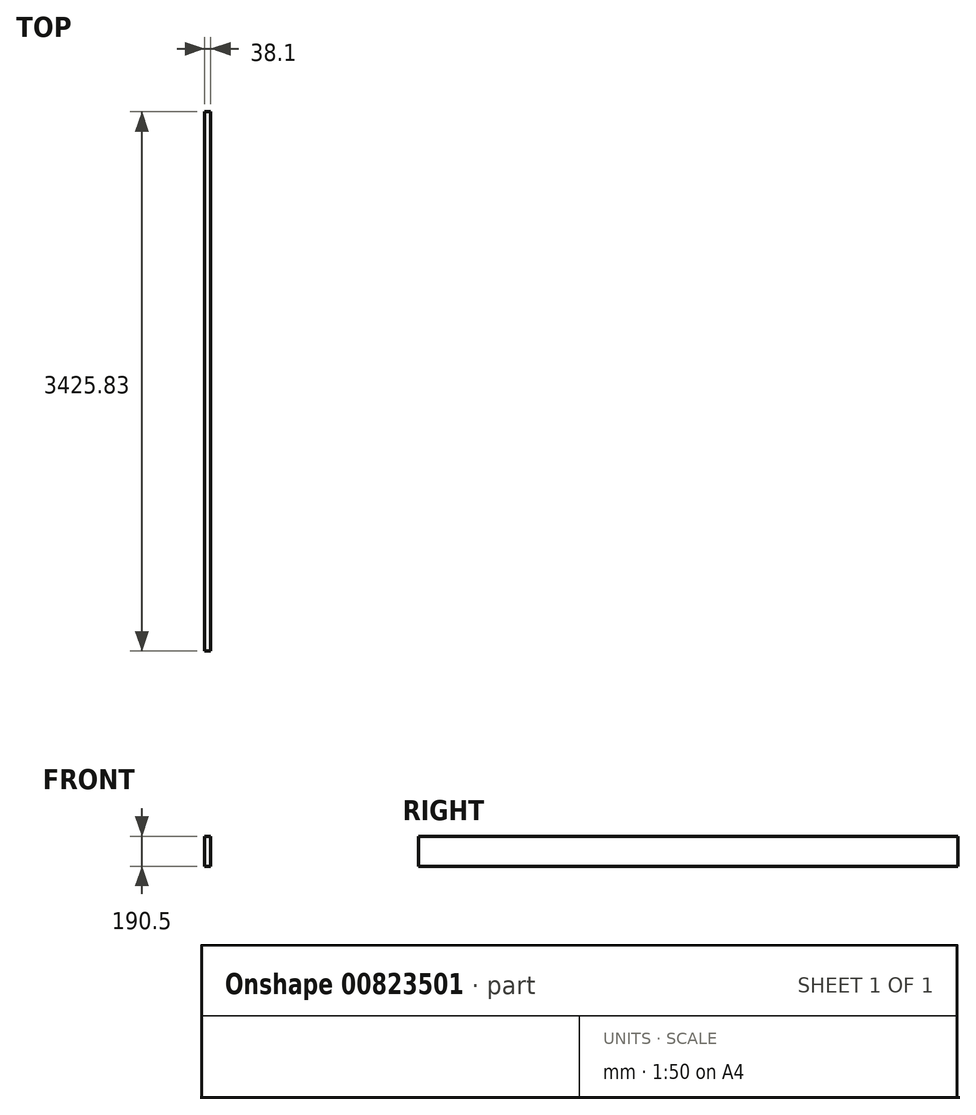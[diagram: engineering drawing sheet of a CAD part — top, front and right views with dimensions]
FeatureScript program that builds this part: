
annotation { "Feature Type Name" : "Feature", "Feature Type Description" : "" }
export const myFeature = defineFeature(function(context is Context, id is Id, definition is map)
    precondition{}
    {
        {
            var Q0;
            Q0=qCreatedBy(makeId("Front.planeOp"),FACE);
            var sketch = newSketch(context, id + "F0", { "sketchPlane" : qUnion([Q0])});
            skLineSegment(sketch, "E0.bottom", {"start": v(0, 0) * mm, "end": v(38.1, 0) * mm});
            skLineSegment(sketch, "E0.top", {"start": v(0, 190.5) * mm, "end": v(38.1, 190.5) * mm});
            skLineSegment(sketch, "E0.left", {"start": v(0, 0) * mm, "end": v(0, 190.5) * mm});
            skLineSegment(sketch, "E0.right", {"start": v(38.1, 0) * mm, "end": v(38.1, 190.5) * mm});
            skSolve(sketch);
        }
        {
            var Q0;
            Q0=qSketchRegion(id+"F0",true);
            extrude(context, id + "F1", {"entities" : qUnion([Q0]), "depth" : 3425.82 * mm, "offsetDistance" : 25.4 * mm});
        }
    });
